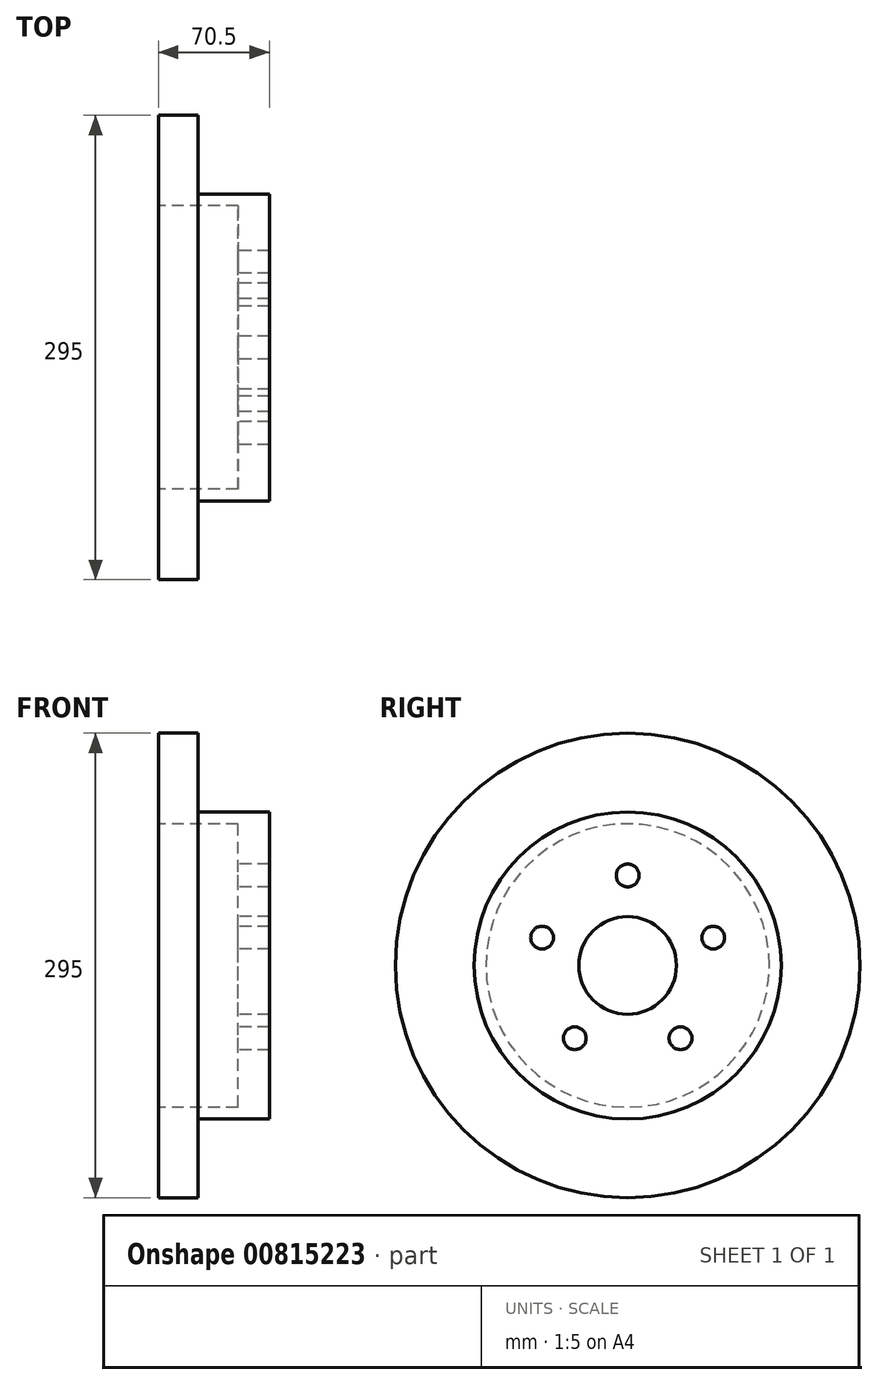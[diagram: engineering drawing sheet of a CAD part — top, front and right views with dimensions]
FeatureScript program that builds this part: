
annotation { "Feature Type Name" : "Feature", "Feature Type Description" : "" }
export const myFeature = defineFeature(function(context is Context, id is Id, definition is map)
    precondition{}
    {
        {
            var Q0;
            Q0=qCreatedBy(makeId("Right.planeOp"),FACE);
            var sketch = newSketch(context, id + "F0", { "sketchPlane" : qUnion([Q0])});
            skCircle(sketch, "E0", {"center": v(0, 0) * mm, "radius": 90 * mm});
            skCircle(sketch, "E1", {"center": v(0, 0) * mm, "radius": 147.5 * mm});
            skCircle(sketch, "E2", {"center": v(0, 0) * mm, "radius": 97.5 * mm});
            skSolve(sketch);
        }
        {
            var Q0;
            Q0 = qSketchRegion(id + "F0", true);
            extrude(context, id + "F1", {"entities" : qUnion([Q0]), "depth" : 25 * mm, "offsetDistance" : 25.4 * mm});
        }
        {
            var Q0;
            Q0=makeQuery(id+"F0.imprint","IMPRINT",FACE,{"disambiguationData":[TD([[makeQuery(id+"F0.imprint","IMPRINT",EDGE,{"derivedFrom":sQuery(id+"F0.wireOp",EDGE,"E0")}),-1.0]])]});
            extrude(context, id + "F2", {"entities" : qUnion([Q0]), "operationType" : NewBodyOperationType.ADD, "depth" : 50.5 * mm, "offsetDistance" : 25.4 * mm});
        }
        {
            var Q0;
            Q0=qCreatedBy(makeId("Right.planeOp"),FACE);
            cPlane(context, id + "F3", {"entities" : qUnion([Q0]), "cplaneType" : CPlaneType.OFFSET, "offset" : 50.5 * mm, "width" : 152.4 * mm, "height" : 152.4 * mm});
        }
        {
            var Q0;
            Q0=qCreatedBy(id+"F3.planeOp",FACE);
            var sketch = newSketch(context, id + "F4", { "sketchPlane" : qUnion([Q0])});
            skCircle(sketch, "E3", {"center": v(0, 0) * mm, "radius": 97.5 * mm});
            skCircle(sketch, "E4", {"center": v(0, 57.15) * mm, "radius": 7.25 * mm});
            skCircle(sketch, "E5.1.0", {"center": v(-54.35, 17.66) * mm, "radius": 7.25 * mm});
            skCircle(sketch, "E5.2.0", {"center": v(-33.6, -46.24) * mm, "radius": 7.25 * mm});
            skCircle(sketch, "E5.3.0", {"center": v(33.6, -46.24) * mm, "radius": 7.25 * mm});
            skCircle(sketch, "E5.4.0", {"center": v(54.35, 17.66) * mm, "radius": 7.25 * mm});
            skCircle(sketch, "E6", {"center": v(0, 0) * mm, "radius": 31 * mm});
            skSolve(sketch);
        }
        {
            var Q0;
            Q0 = qSketchRegion(id + "F4", true);
            extrude(context, id + "F5", {"entities" : qUnion([Q0]), "operationType" : NewBodyOperationType.ADD, "depth" : 20 * mm, "offsetDistance" : 25.4 * mm});
        }
    });
